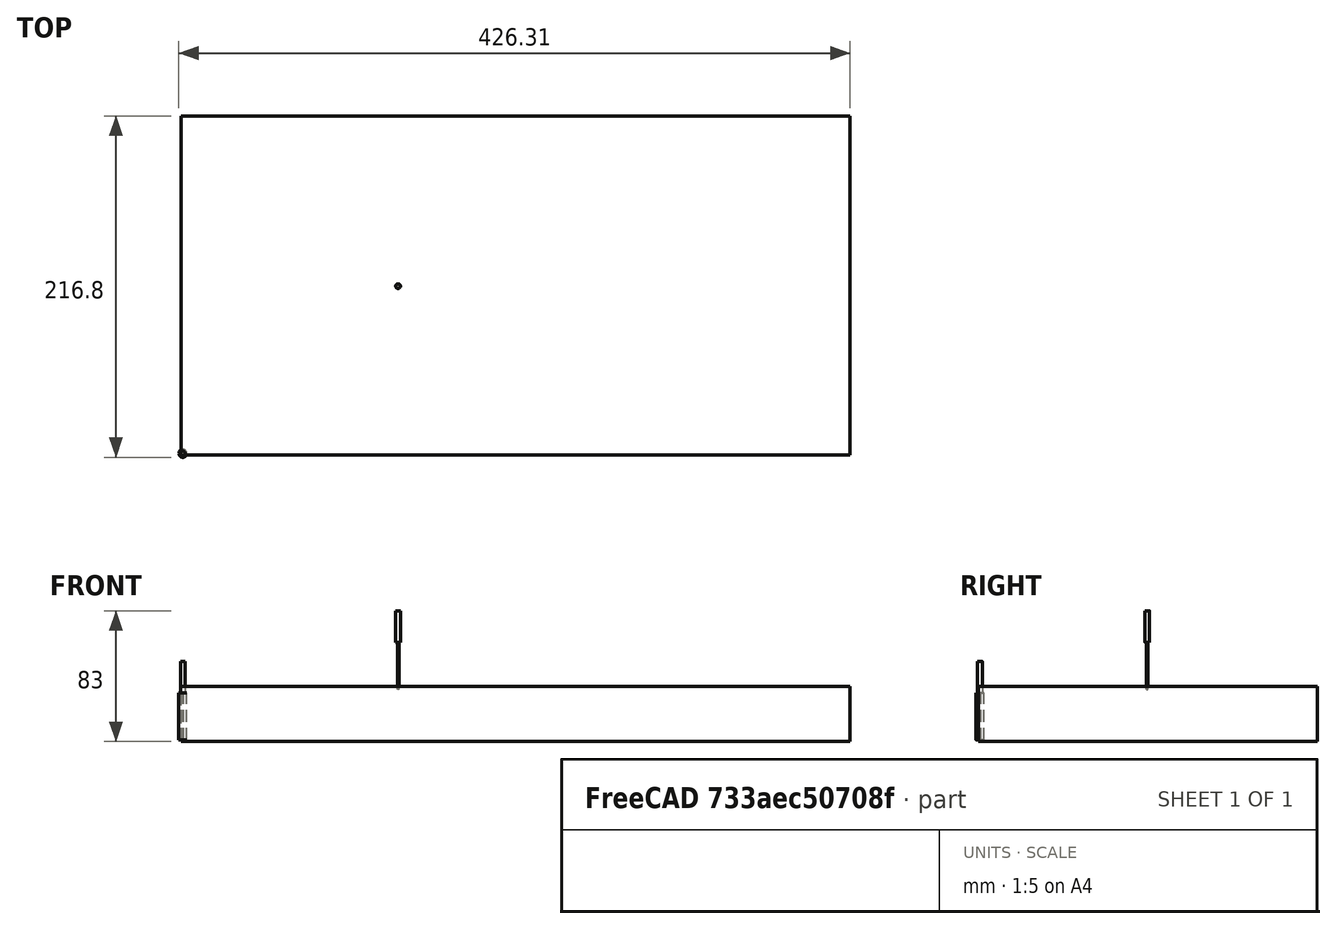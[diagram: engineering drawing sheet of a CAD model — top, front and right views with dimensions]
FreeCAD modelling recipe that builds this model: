
FCSTD DOCUMENT  (FreeCAD 0.19R24212 (Git))
Label: path preview
License: Creative Commons Attribution
LicenseURL: http://creativecommons.org/licenses/by/4.0/
objects: Path::FeaturePython×8, Part::FeaturePython×5, App::DocumentObjectGroup×2, Mesh::FeaturePython×2, Sketcher::SketchObject×1, PartDesign::Pad×1, Part::Part2DObjectPython×1, PartDesign::SubShapeBinder×1, PartDesign::Pocket×1, PartDesign::Body×1, App::FeaturePython×1, Path::FeatureCompoundPython×1
note: 17 computed .brp shape members not serialized (recipe doc carries the construction recipe); baked Part::Feature solids carry a one-line shape summary decoded from their .brp

FEATURE [Sketcher::SketchObject] Sketch
  FullyConstrained = false
  MapMode = 5
  Support = -> [XY_Plane]
  sketch-geometry (4):
    g0: LineSegment StartX=0 StartY=0 StartZ=0 EndX=422.81 EndY=0 EndZ=0
    g1: LineSegment StartX=422.81 StartY=0 StartZ=0 EndX=422.81 EndY=213.305 EndZ=0
    g2: LineSegment StartX=422.81 StartY=213.305 StartZ=0 EndX=0 EndY=213.305 EndZ=0
    g3: LineSegment StartX=0 StartY=213.305 StartZ=0 EndX=0 EndY=0 EndZ=0
  constraints (9):
    c: Coincident(g0,g1)
    c: Coincident(g1,g2)
    c: Coincident(g2,g3)
    c: Coincident(g3,g0)
    c: Horizontal(g0)
    c: Horizontal(g2)
    c: Vertical(g1)
    c: Vertical(g3)
    c: Coincident(g0,g-1)
FEATURE [PartDesign::Pad] Pad
  Direction = (1,1,1)
  Length = 33
  Length2 = 100
  Profile = -> Sketch
  Refine = true
  Type = 0
FEATURE [Part::Part2DObjectPython] ShapeString  # Draft 2D object (typed FeaturePython)
  FontFile = <path>
  Placement = pos=(17.613,75.706,33) rot=(0,0,1;0rad)
  Size = 23
  String = Atelier Path !
  Tracking = 0
FEATURE [PartDesign::SubShapeBinder] Binder
  BindMode = 0
  ClaimChildren = false
  Context = -> Body [Binder.]
  Fuse = false
  MakeFace = true
  PartialLoad = false
  Relative = true
  Support = -> [ShapeString]
  _Version = 2
FEATURE [PartDesign::Pocket] Pocket
  BaseFeature = -> Pad
  Length = 1
  Length2 = 100
  Profile = -> Binder
  Refine = true
  Type = 0
FEATURE [PartDesign::Body] Body
  Group = -> [Sketch,Pad,Binder,Pocket]
  Origin = -> Origin
  Tip = -> Pocket
FEATURE [App::FeaturePython] SetupSheet  # Path/CAM operation (typed FeaturePython)
  ClearanceHeightExpression = OpStockZMax+SetupSheet.ClearanceHeightOffset
  ClearanceHeightOffset = 5
  CoolantMode = 0
  CoolantModes = None | Flood | Mist
  FinalDepthExpression = OpFinalDepth
  HorizRapid = 0
  SafeHeightExpression = OpStockZMax+SetupSheet.SafeHeightOffset
  SafeHeightOffset = 3
  StartDepthExpression = OpStartDepth
  StepDownExpression = OpToolDiameter
  VertRapid = 0
FEATURE [Part::FeaturePython] Clone  label="Model-Body"  # Draft clone (typed FeaturePython)
  AttacherType = Attacher::AttachEngine3D
  Fuse = false
  Objects = -> [Body]
  PathResource = Model
  Scale = (1,1,1)
FEATURE [App::DocumentObjectGroup] Model
  Group = -> [Clone]
FEATURE [Part::FeaturePython] ToolBit  label="Endmill"  # Path/CAM toolbit (typed FeaturePython)
  BitPropertyNames = Chipload | CuttingEdgeHeight | Diameter | Flutes | Length | Material | ShankDiameter
  BitShape = <path>
  Chipload = 0
  CuttingEdgeHeight = 30
  Diameter = 5
  Flutes = 0
  Length = 50
  Material = 0
  ShankDiameter = 3
  ShapeName = endmill
FEATURE [Path::FeaturePython] TC__Default_Tool  label="TC: Default Tool"  # Path/CAM operation (typed FeaturePython)
  HorizFeed = 0
  HorizRapid = 0
  SpindleDir = 0
  SpindleSpeed = 0
  Tool = -> ToolBit
  ToolNumber = 1
  VertFeed = 0
  VertRapid = 0
  expr: VertRapid = SetupSheet.VertRapid
  expr: HorizRapid = SetupSheet.HorizRapid
FEATURE [Part::FeaturePython] Stock  # WARN: FeaturePython — macro-defined, semantics opaque (R4)
  Base = -> Model
  ExtXneg = 1
  ExtXpos = 1
  ExtYneg = 1
  ExtYpos = 1
  ExtZneg = 1
  ExtZpos = 1
  StockType = FromBase
FEATURE [Part::FeaturePython] ToolBit001  label="1mm_Endmill"  # Path/CAM toolbit (typed FeaturePython)
  BitPropertyNames = Chipload | CuttingEdgeHeight | Diameter | Flutes | Length | Material | ShankDiameter
  BitShape = <path>
  Chipload = 0
  CuttingEdgeHeight = 30
  Diameter = 1
  File = <userpath>/.FreeCAD/Toolbit/Bit/1mm_Endmill.fctb
  Flutes = 0
  Length = 50
  Material = 0
  ShankDiameter = 3
  ShapeName = endmill
FEATURE [Path::FeaturePython] TC__1mm_Endmill  label="TC: 1mm_Endmill"  # Path/CAM operation (typed FeaturePython)
  HorizFeed = 0
  HorizRapid = 0
  SpindleDir = 0
  SpindleSpeed = 0
  Tool = -> ToolBit001
  ToolNumber = 10
  VertFeed = 0
  VertRapid = 0
  expr: HorizRapid = SetupSheet.HorizRapid
  expr: VertRapid = SetupSheet.VertRapid
FEATURE [App::DocumentObjectGroup] Tools
  Group = -> [TC__Default_Tool,TC__1mm_Endmill]
FEATURE [Path::FeaturePython] Pocket_Shape  # Path/CAM operation (typed FeaturePython)
  Active = true
  AreaParams:
    Tolerance = 1e-07
    FitArcs = True
    Simplify = False
    CleanDistance = 0.0
    Accuracy = 0.01
    Unit = 1.0
    MinArcPoints = 4
    MaxArcPoints = 100
    ClipperScale = 10000000.0
    Fill = 0
    Coplanar = 0
    Reorient = True
    Outline = False
    Explode = False
    OpenMode = 0
    Deflection = 0.01
    SubjectFill = 0
    ClipFill = 0
    Offset = 0.0
    ExtraPass = 0
    Stepover = 0.0
    LastStepover = 0.0
    JoinType = 0
    EndType = 0
    MiterLimit = 2.0
    RoundPrecision = 0.0
    PocketMode = 1
    ToolRadius = 0.5
    PocketExtraOffset = 0.0
    PocketStepover = 1.0
    PocketLastStepover = 0.0
    FromCenter = True
    Angle = 45.0
    AngleShift = 0.0
    Shift = 0.0
    Thicken = False
    SectionCount = -1
    Stepdown = 1.0
    SectionOffset = 0.0
    SectionTolerance = 1e-06
    SectionMode = 2
    Project = False
  AttemptInverseAngle = true
  Base = -> [Clone]
  ClearanceHeight = 39
  CoolantMode = None
  CutMode = 0
  CycleTime = Erreur de temps de cycle
  EnableRotation = 0
  ExtensionCorners = true
  ExtensionLengthDefault = 0.5
  ExtraOffset = 0
  FinalDepth = 32
  FinishDepth = 0
  InverseAngle = false
  KeepToolDown = false
  LimitDepthToFace = true
  MinTravel = false
  OffsetPattern = 0
  OpFinalDepth = 32
  OpStartDepth = 34
  OpStockZMax = 34
  OpStockZMin = -1
  OpToolDiameter = 1
  PathParams = {'orientation': 1, 'feedrate': 0.0, 'feedrate_v': 0.0, 'verbose': True, 'resume_height': 37.0, 'retraction': 39.0, 'return_end': True, 'preamble': False}
  ReverseDirection = false
  SafeHeight = 37
  StartAt = 0
  StartDepth = 34
  StartPoint = (0,0,0)
  StepDown = 1
  StepOver = 100
  ToolController = -> TC__1mm_Endmill
  UseOutline = false
  UseStartPoint = false
  ZigZagAngle = 45
  expr: ExtensionLengthDefault = OpToolDiameter / 2
  expr: ClearanceHeight = OpStockZMax + SetupSheet.ClearanceHeightOffset
  expr: SafeHeight = OpStockZMax + SetupSheet.SafeHeightOffset
  expr: StepDown = OpToolDiameter
  expr: FinalDepth = OpFinalDepth
  expr: StartDepth = OpStartDepth
FEATURE [Path::FeaturePython] Pocket_Shape001  # Path/CAM operation (typed FeaturePython)
  Active = true
  AreaParams:
    Tolerance = 1e-07
    FitArcs = True
    Simplify = False
    CleanDistance = 0.0
    Accuracy = 0.01
    Unit = 1.0
    MinArcPoints = 4
    MaxArcPoints = 100
    ClipperScale = 10000000.0
    Fill = 0
    Coplanar = 0
    Reorient = True
    Outline = False
    Explode = False
    OpenMode = 0
    Deflection = 0.01
    SubjectFill = 0
    ClipFill = 0
    Offset = 0.0
    ExtraPass = 0
    Stepover = 0.0
    LastStepover = 0.0
    JoinType = 0
    EndType = 0
    MiterLimit = 2.0
    RoundPrecision = 0.0
    PocketMode = 1
    ToolRadius = 0.5
    PocketExtraOffset = 0.0
    PocketStepover = 1.0
    PocketLastStepover = 0.0
    FromCenter = True
    Angle = 45.0
    AngleShift = 0.0
    Shift = 0.0
    Thicken = False
    SectionCount = -1
    Stepdown = 1.0
    SectionOffset = 0.0
    SectionTolerance = 1e-06
    SectionMode = 2
    Project = False
  AttemptInverseAngle = true
  Base = -> [Clone]
  ClearanceHeight = 39
  CoolantMode = None
  CutMode = 0
  CycleTime = Erreur de temps de cycle
  EnableRotation = 0
  ExtensionCorners = true
  ExtensionLengthDefault = 0.5
  ExtraOffset = 0
  FinalDepth = 32
  FinishDepth = 0
  InverseAngle = false
  KeepToolDown = false
  LimitDepthToFace = true
  MinTravel = false
  OffsetPattern = 0
  OpFinalDepth = 32
  OpStartDepth = 34
  OpStockZMax = 34
  OpStockZMin = -1
  OpToolDiameter = 1
  PathParams = {'orientation': 1, 'feedrate': 0.0, 'feedrate_v': 0.0, 'verbose': True, 'resume_height': 37.0, 'retraction': 39.0, 'return_end': True, 'preamble': False}
  ReverseDirection = false
  SafeHeight = 37
  StartAt = 0
  StartDepth = 34
  StartPoint = (0,0,0)
  StepDown = 1
  StepOver = 100
  ToolController = -> TC__1mm_Endmill
  UseOutline = false
  UseStartPoint = false
  ZigZagAngle = 45
  expr: ExtensionLengthDefault = OpToolDiameter / 2
  expr: ClearanceHeight = OpStockZMax + SetupSheet.ClearanceHeightOffset
  expr: SafeHeight = OpStockZMax + SetupSheet.SafeHeightOffset
  expr: StepDown = OpToolDiameter
  expr: FinalDepth = OpFinalDepth
  expr: StartDepth = OpStartDepth
FEATURE [Path::FeaturePython] Profile  # Path/CAM operation (typed FeaturePython)
  Active = true
  AreaParams:
    Tolerance = 1e-07
    FitArcs = True
    Simplify = False
    CleanDistance = 0.0
    Accuracy = 0.01
    Unit = 1.0
    MinArcPoints = 4
    MaxArcPoints = 100
    ClipperScale = 10000000.0
    Fill = 0
    Coplanar = 0
    Reorient = True
    Outline = False
    Explode = False
    OpenMode = 0
    Deflection = 0.01
    SubjectFill = 0
    ClipFill = 0
    Offset = -0.5
    ExtraPass = 0
    Stepover = 0.0
    LastStepover = 0.0
    JoinType = 0
    EndType = 0
    MiterLimit = 2.0
    RoundPrecision = 0.0
    PocketMode = 0
    ToolRadius = 1.0
    PocketExtraOffset = 0.0
    PocketStepover = 0.0
    PocketLastStepover = 0.0
    FromCenter = False
    Angle = 45.0
    AngleShift = 0.0
    Shift = 0.0
    Thicken = False
    SectionCount = -1
    Stepdown = 1.0
    SectionOffset = 0.0
    SectionTolerance = 1e-06
    SectionMode = 2
    Project = False
  AttemptInverseAngle = true
  Base = -> [Clone]
  ClearanceHeight = 39
  CoolantMode = None
  CycleTime = Erreur de temps de cycle
  Direction = 0
  EnableRotation = 0
  FinalDepth = 32
  HandleMultipleFeatures = 0
  InverseAngle = false
  JoinType = 0
  LimitDepthToFace = true
  MiterLimit = 0.1
  OffsetExtra = 0
  OpFinalDepth = 32
  OpStartDepth = 34
  OpStockZMax = 34
  OpStockZMin = -1
  OpToolDiameter = 1
  PathParams = {'orientation': 1, 'feedrate': 0.0, 'feedrate_v': 0.0, 'verbose': True, 'resume_height': 37.0, 'retraction': 39.0, 'return_end': True, 'preamble': False}
  ReverseDirection = false
  SafeHeight = 37
  Side = 1
  StartDepth = 34
  StartPoint = (0,0,0)
  StepDown = 1
  ToolController = -> TC__1mm_Endmill
  UseComp = true
  UseStartPoint = false
  processCircles = false
  processHoles = false
  processPerimeter = true
  expr: ClearanceHeight = OpStockZMax + SetupSheet.ClearanceHeightOffset
  expr: SafeHeight = OpStockZMax + SetupSheet.SafeHeightOffset
  expr: StepDown = OpToolDiameter
  expr: FinalDepth = OpFinalDepth
  expr: StartDepth = OpStartDepth
FEATURE [Path::FeaturePython] Profile001  # Path/CAM operation (typed FeaturePython)
  Active = true
  AreaParams:
    Tolerance = 1e-07
    FitArcs = True
    Simplify = False
    CleanDistance = 0.0
    Accuracy = 0.01
    Unit = 1.0
    MinArcPoints = 4
    MaxArcPoints = 100
    ClipperScale = 10000000.0
    Fill = 0
    Coplanar = 0
    Reorient = True
    Outline = False
    Explode = False
    OpenMode = 0
    Deflection = 0.01
    SubjectFill = 0
    ClipFill = 0
    Offset = 0.5
    ExtraPass = 0
    Stepover = 0.0
    LastStepover = 0.0
    JoinType = 0
    EndType = 0
    MiterLimit = 2.0
    RoundPrecision = 0.0
    PocketMode = 0
    ToolRadius = 1.0
    PocketExtraOffset = 0.0
    PocketStepover = 0.0
    PocketLastStepover = 0.0
    FromCenter = False
    Angle = 45.0
    AngleShift = 0.0
    Shift = 0.0
    Thicken = False
    SectionCount = -1
    Stepdown = 1.0
    SectionOffset = 0.0
    SectionTolerance = 1e-06
    SectionMode = 2
    Project = False
  AttemptInverseAngle = true
  Base = -> [Clone]
  ClearanceHeight = 39
  CoolantMode = None
  CycleTime = Erreur de temps de cycle
  Direction = 0
  EnableRotation = 0
  FinalDepth = 32
  HandleMultipleFeatures = 0
  InverseAngle = false
  JoinType = 0
  LimitDepthToFace = true
  MiterLimit = 0.1
  OffsetExtra = 0
  OpFinalDepth = 32
  OpStartDepth = 34
  OpStockZMax = 34
  OpStockZMin = -1
  OpToolDiameter = 1
  PathParams = {'orientation': 1, 'feedrate': 0.0, 'feedrate_v': 0.0, 'verbose': True, 'resume_height': 37.0, 'retraction': 39.0, 'return_end': True, 'preamble': False}
  ReverseDirection = false
  SafeHeight = 37
  Side = 0
  StartDepth = 34
  StartPoint = (0,0,0)
  StepDown = 1
  ToolController = -> TC__1mm_Endmill
  UseComp = true
  UseStartPoint = false
  processCircles = false
  processHoles = false
  processPerimeter = true
  expr: ClearanceHeight = OpStockZMax + SetupSheet.ClearanceHeightOffset
  expr: SafeHeight = OpStockZMax + SetupSheet.SafeHeightOffset
  expr: StepDown = OpToolDiameter
  expr: FinalDepth = OpFinalDepth
  expr: StartDepth = OpStartDepth
FEATURE [Path::FeaturePython] Adaptive  # Path/CAM operation (typed FeaturePython)
  Active = true
  Base = -> [Clone]
  ClearanceHeight = 39
  CoolantMode = None
  CycleTime = Erreur de temps de cycle
  FinalDepth = 32
  FinishDepth = 0
  FinishingProfile = true
  ForceInsideOut = false
  HelixAngle = 5
  HelixConeAngle = 0
  HelixDiameterLimit = 0
  KeepToolDownRatio = 3
  LiftDistance = 0
  OpFinalDepth = 32
  OpStartDepth = 34
  OpStockZMax = 34
  OpStockZMin = -1
  OpToolDiameter = 1
  OperationType = 0
  SafeHeight = 37
  Side = 1
  StartDepth = 34
  StepDown = 1
  StepOver = 20
  StockToLeave = 0
  StopProcessing = false
  Stopped = false
  Tolerance = 0.1
  ToolController = -> TC__1mm_Endmill
  UseHelixArcs = false
  UseOutline = false
  expr: ClearanceHeight = OpStockZMax + SetupSheet.ClearanceHeightOffset
  expr: SafeHeight = OpStockZMax + SetupSheet.SafeHeightOffset
  expr: StepDown = OpToolDiameter
  expr: FinalDepth = OpFinalDepth
  expr: StartDepth = OpStartDepth
FEATURE [Path::FeatureCompoundPython] Operations  # Path/CAM operation (typed FeaturePython)
  Group = -> [Pocket_Shape,Pocket_Shape001,Profile,Profile001,Adaptive]
  UsePlacements = false
FEATURE [Path::FeaturePython] Job  # Path/CAM operation (typed FeaturePython)
  CycleTime = 00:00:00
  Fixtures = G54
  GeometryTolerance = 0.01
  Model = -> Model
  Operations = -> Operations
  OrderOutputBy = 0
  PostProcessor = 1
  SetupSheet = -> SetupSheet
  SplitOutput = false
  Stock = -> Stock
  Tools = -> Tools
FEATURE [Part::FeaturePython] CutTool  # WARN: FeaturePython — macro-defined, semantics opaque (R4)
  Placement = pos=(136.773,106.185,32) rot=(0,0,1;0rad)
FEATURE [Mesh::FeaturePython] CutMaterial  # WARN: FeaturePython — macro-defined, semantics opaque (R4)
FEATURE [Mesh::FeaturePython] CutMaterialIn  # WARN: FeaturePython — macro-defined, semantics opaque (R4)
note: 3 file-system paths scrubbed to <path> (originals preserved in the JSON sidecar)
